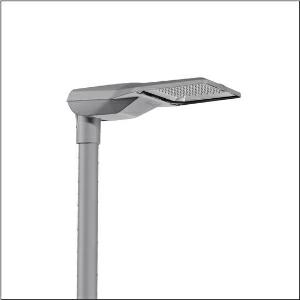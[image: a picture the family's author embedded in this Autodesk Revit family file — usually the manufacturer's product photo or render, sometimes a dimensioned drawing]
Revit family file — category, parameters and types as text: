
# Revit family: streetlight_sl_21_midi___pl52_5xe7h33a08mb_cac4
name_source: partatom
category: Lighting Fixtures
units: mm (PartAtom-declared; Revit-internal decimal feet)

## family parameters
Cut with Voids When Loaded = No
Host = Face
Light Source = No
Part Type = Normal
Room Calculation Point = No
Round Connector Dimension = Use Diameter
Shared = No

## types (1)
- --- (1 x LED, 17960 lm, 136 W, 3000K)
    Apparent Load = 136 VA
    CIE Flux Codes = 27 59 98 100 100
    Color Rendering = 70
    Color Temperature = 3000K
    Default Elevation = 1800 mm
    Description = Streetlight SL 21 midi, mast luminaire, primary light control with lens, of PMMA, primary optical cover: cover, of toughened safety glass, transparent, light distribution: PL52, light emission: direct distribution, primary light characteristic: asymmetric, installation type: post-top, side-entry, LED, 3G 1.5mm², High Power LED, rated luminous flux: 17.960lm, luminous efficacy: 132lm/W, light colour: 730, colour temperature: 3000K, control: overheat protection, constant luminous flux control, time-dependent luminous flux control, flexible luminous flux parameterisation, mains connection: 220..240V, AC, 50/60Hz, connection cable pre-assembled, cable length: 12,5m, wiring characteristics: H07RN-F, start of lifetime: 136W, end of service life: 142W, reduction: 61W, luminaire housing, of diecast aluminium, powder-coated, Siteco® metallic grey (DB 702S), corrosivity category C5 mid according to DIN EN ISO 12944, please order mast flange separately, inclination adjustable: 0°, 5°, 10°, 15°, sealing non-destructively replaceable, multi-level sealing system, length: 644mm, width: 335mm, height: 110mm, mast flange for spigot size: 42mm (side-entry): 5XC10008XM4, 60/48mm (side-entry/post-top): 5XC10108XM2, 76/60mm (side-entry/post-top): 5XC10108XM1, protection rating (complete): IP66, insulation class (complete): insulation class II (safety insulation), certification: CE, ENEC, ENEC+, VDE, impact resistance: IK09, permissible operating ambient temperature for outdoor applications: -40..+50°C, standard-compliant lighting for roads and squares, packaging unit: 1 piece

Light Distribution: PL52
    Height = 111 mm
    Lamp = 1 x LED
    Lamp Light Flux = 17960 lm
    Lamp Power = 136 W
    Lamp count = 1
    Length = 644 mm
    Luminous efficacy = 132 lm/W
    Manufacturer = Siteco
    ModVariant = No
    Model = 5XE7H33A08MB
    Number of Poles = 1
    OnlyDefault = Yes
    Power Factor = 1
    Product Name = Streetlight SL 21 midi | PL52
    Product group = mast luminaire | pylon top
    ProductGroupID = 6100
    Protection Class = Protection class II
    Protection Degree = IP 66
    RLX_Detail_Level = 1
    RLX_Emergency_Light_Flux = 0 lm
    RLX_Emergency_Type = 0
    RLX_Emergency_Type_DB = No
    RlxData = <blob elided: 100301 chars, md5=e87186bc>
    Socket = socket
    Standby Power = 0 W
    System Light Flux = 17960 lm
    System Power = 136 W
    Type Comments = factory setting: luminous flux: 100 % | Output Level: 100 % | 695 mA
    Type Image = l_1004298.jpg
    URL = http://relux.com
    VarID = @adj_142757
    Voltage = 0 V
    Weight = 0.00 kg
    Width = 336 mm

## geometry (parser evidence)
native form markers: Blend x4, Sweep x10
no freeform markers — native parametric forms only
